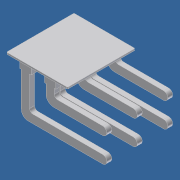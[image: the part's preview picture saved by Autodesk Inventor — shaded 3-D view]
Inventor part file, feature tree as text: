
AUTODESK INVENTOR PART (.ipt)
format: ipt  version: 2014 (Build 180170000, 170)  size: 180,224 bytes
history: native  units: in
note: dims shown in document units (in); Inventor stores cm internally (conversion verified against a paired STEP export)
features: other x8, extrude x3, sketch x3, pattern_linear x2
ambient origin geometry x8: Origin, YZ Plane, XZ Plane, XY Plane, X Axis, Y Axis, Z Axis, Center Point
bodies: Solid1 (feature_tree)
feature tree (16):
  other  "M202830_terminal_angW"
  extrude  "Extrusion1"  Depth=0.03in TaperAngle=0.0deg
  extrude  "Extrusion2"  Depth=0.03in TaperAngle=0.0deg
  pattern_linear  "Rectangular Pattern1"  Count1=3 Spacing1=0.185in
  extrude  "Extrusion3"  [1 undecoded]
  pattern_linear  "Rectangular Pattern2"  [2 undecoded]
  other  "to_base_XY"
  other  "to_base_YZ"
  other  "to_base_ZX"
  other  "to_base_X"
  other  "to_base_Y"
  other  "to_base_Z"
  other  "to_base_Center"
  sketch  "Sketch_2"  dims[d4=1.1811in d6=0.185in d7=0.3937in d9=0.0in d10=0.03in d11=0.0in d12=1.1811in d14=0.185in d15=0.3937in d17=0.0in]
  sketch  "Sketch_1"  dims[d0=0.01in d1=0.0in d2=0.03in d3=0.0in]
  sketch  "Sketch_18"
note: 3 required parameter values undecoded (feature->parameter linkage not recoverable at this tier; creation-order binding heuristic only, values carry confidence <= 0.55)
